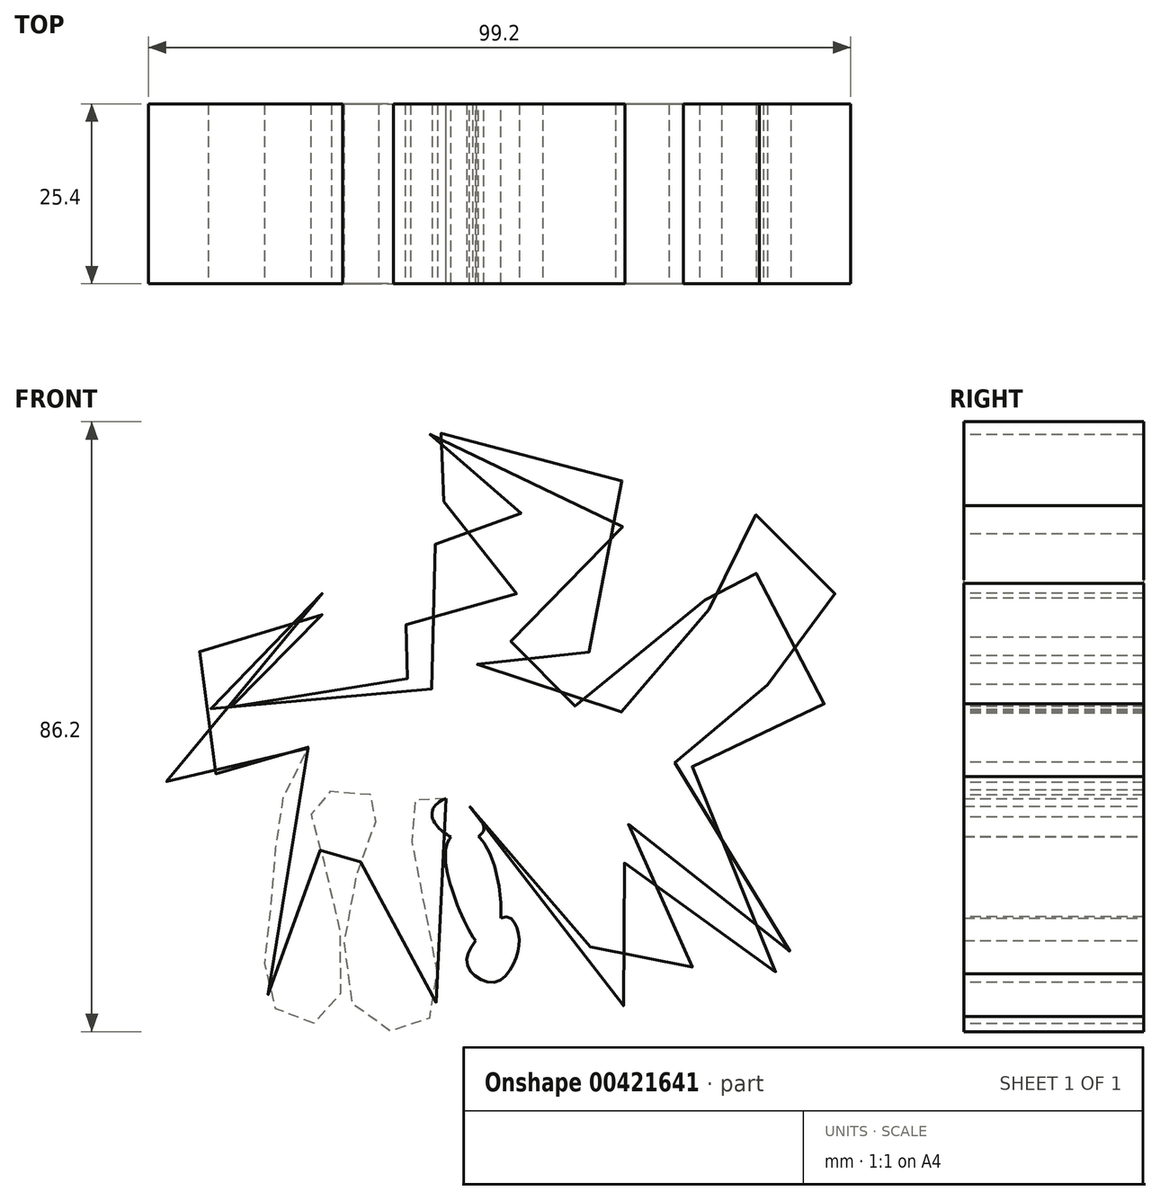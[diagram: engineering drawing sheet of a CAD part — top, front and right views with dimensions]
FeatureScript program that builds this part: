
annotation { "Feature Type Name" : "Feature", "Feature Type Description" : "" }
export const myFeature = defineFeature(function(context is Context, id is Id, definition is map)
    precondition{}
    {
        {
            var Q0;
            Q0=qCreatedBy(makeId("Front.planeOp"),FACE);
            var sketch = newSketch(context, id + "F0", { "sketchPlane" : qUnion([Q0])});
            skFitSpline(sketch, "E0", {"points": [v(-24.68, 12.83) * mm, v(-33.88, 23.4) * mm, v(-26.05, 37.12) * mm, v(-17.24, 28.1) * mm, v(-16.26, 38.88) * mm, v(-34.86, 43.38) * mm, v(-34.47, 50.63) * mm, v(-31.53, 51.22) * mm, v(-7.05, 52) * mm, v(-3.53, 39.27) * mm, v(-4.7, 23.01) * mm, v(-14.1, 20.27) * mm, v(-22.52, 22.43) * mm, v(-24.1, 18.9) * mm, v(-19.78, 15.38) * mm, v(-7.44, 12.44) * mm, v(8.81, 14.2) * mm, v(8.62, 26.74) * mm, v(5.68, 37.7) * mm, v(15.08, 40.25) * mm, v(15.86, 29.09) * mm, v(25.46, 29.67) * mm, v(26.25, 13.42) * mm, v(16.84, 15.77) * mm, v(15.86, 3.62) * mm, v(3.13, 4.8) * mm, v(19.78, -17.53) * mm, v(15.47, -24.78) * mm, v(-3.92, -2.84) * mm, v(0, -16.16) * mm, v(7.25, -27.32) * mm, v(-2.35, -30.26) * mm, v(-14.1, -5.39) * mm, v(-23.7, -1.66) * mm, v(-32.32, 0) * mm, v(-31.93, -13.61) * mm, v(-31.14, -31.63) * mm, v(-40.74, -30.65) * mm, v(-40.15, -8.13) * mm, v(-38.58, 0) * mm, v(-46.62, 0) * mm, v(-45.44, -10.09) * mm, v(-44.85, -30.85) * mm, v(-52.69, -29.67) * mm, v(-52.88, -13.22) * mm, v(-50.34, 2.84) * mm, v(-44.66, 12.05) * mm, v(-58.37, 4.4) * mm, v(-70.12, 3.82) * mm, v(-58.17, 24.97) * mm, v(-43.09, 28.1) * mm, v(-53.86, 21.25) * mm, v(-61.9, 12.63) * mm, v(-50.92, 15.77) * mm, v(-40.54, 18.7) * mm, v(-24.68, 12.83) * mm]});
            skSolve(sketch);
        }
        {
            var Q0;
            Q0 = qSketchRegion(id + "F0", true);
            extrude(context, id + "F1", {"entities" : qUnion([Q0]), "depth" : 25.4 * mm});
        }
        {
            var Q0;
            Q0=qCreatedBy(makeId("Front.planeOp"),FACE);
            var sketch = newSketch(context, id + "F2", { "sketchPlane" : qUnion([Q0])});
            skCircle(sketch, "E1", {"center": v(13.71, 35.94) * mm, "radius": 1.58 * mm});
            skSolve(sketch);
        }
        {
            var Q0;
            Q0 = qSketchRegion(id + "F2", true);
            extrude(context, id + "F3", {"entities" : qUnion([Q0]), "operationType" : NewBodyOperationType.REMOVE, "oppositeDirection" : true, "depth" : 23.62 * mm});
        }
        {
            var Q0;
            Q0=qCreatedBy(makeId("Front.planeOp"),FACE);
            var sketch = newSketch(context, id + "F4", { "sketchPlane" : qUnion([Q0])});
            skFitSpline(sketch, "E2", {"points": [v(-27.22, 0) * mm, v(-30.36, -1.86) * mm, v(-28.8, -5) * mm, v(-25.07, -5.97) * mm, v(-23.11, -4.6) * mm, v(-24.48, -2.06) * mm, v(-27.22, 0) * mm]});
            skSolve(sketch);
        }
        {
            var Q0;
            Q0 = qSketchRegion(id + "F4", true);
            extrude(context, id + "F5", {"entities" : qUnion([Q0]), "operationType" : NewBodyOperationType.ADD, "depth" : 25.4 * mm});
        }
        {
            var Q0;
            Q0=qCreatedBy(makeId("Front.planeOp"),FACE);
            var sketch = newSketch(context, id + "F6", { "sketchPlane" : qUnion([Q0])});
            skFitSpline(sketch, "E3", {"points": [v(-28, -5.97) * mm, v(-26.64, -15.77) * mm, v(-22.72, -21.45) * mm, v(-20.76, -17.73) * mm, v(-24.1, -5.39) * mm, v(-28, -5.97) * mm]});
            skSolve(sketch);
        }
        {
            var Q0;
            Q0 = qSketchRegion(id + "F6", true);
            extrude(context, id + "F7", {"entities" : qUnion([Q0]), "operationType" : NewBodyOperationType.ADD, "depth" : 25.4 * mm});
        }
        {
            var Q0;
            Q0=qCreatedBy(makeId("Front.planeOp"),FACE);
            var sketch = newSketch(context, id + "F8", { "sketchPlane" : qUnion([Q0])});
            skFitSpline(sketch, "E4", {"points": [v(-24.29, -20.27) * mm, v(-25.27, -24.19) * mm, v(-21.54, -26.15) * mm, v(-18.6, -22.82) * mm, v(-18.22, -19.3) * mm, v(-19.78, -16.94) * mm, v(-24.29, -20.27) * mm]});
            skSolve(sketch);
        }
        {
            var Q0;
            Q0 = qSketchRegion(id + "F8", true);
            extrude(context, id + "F9", {"entities" : qUnion([Q0]), "operationType" : NewBodyOperationType.ADD, "depth" : 25.4 * mm});
        }
    });
